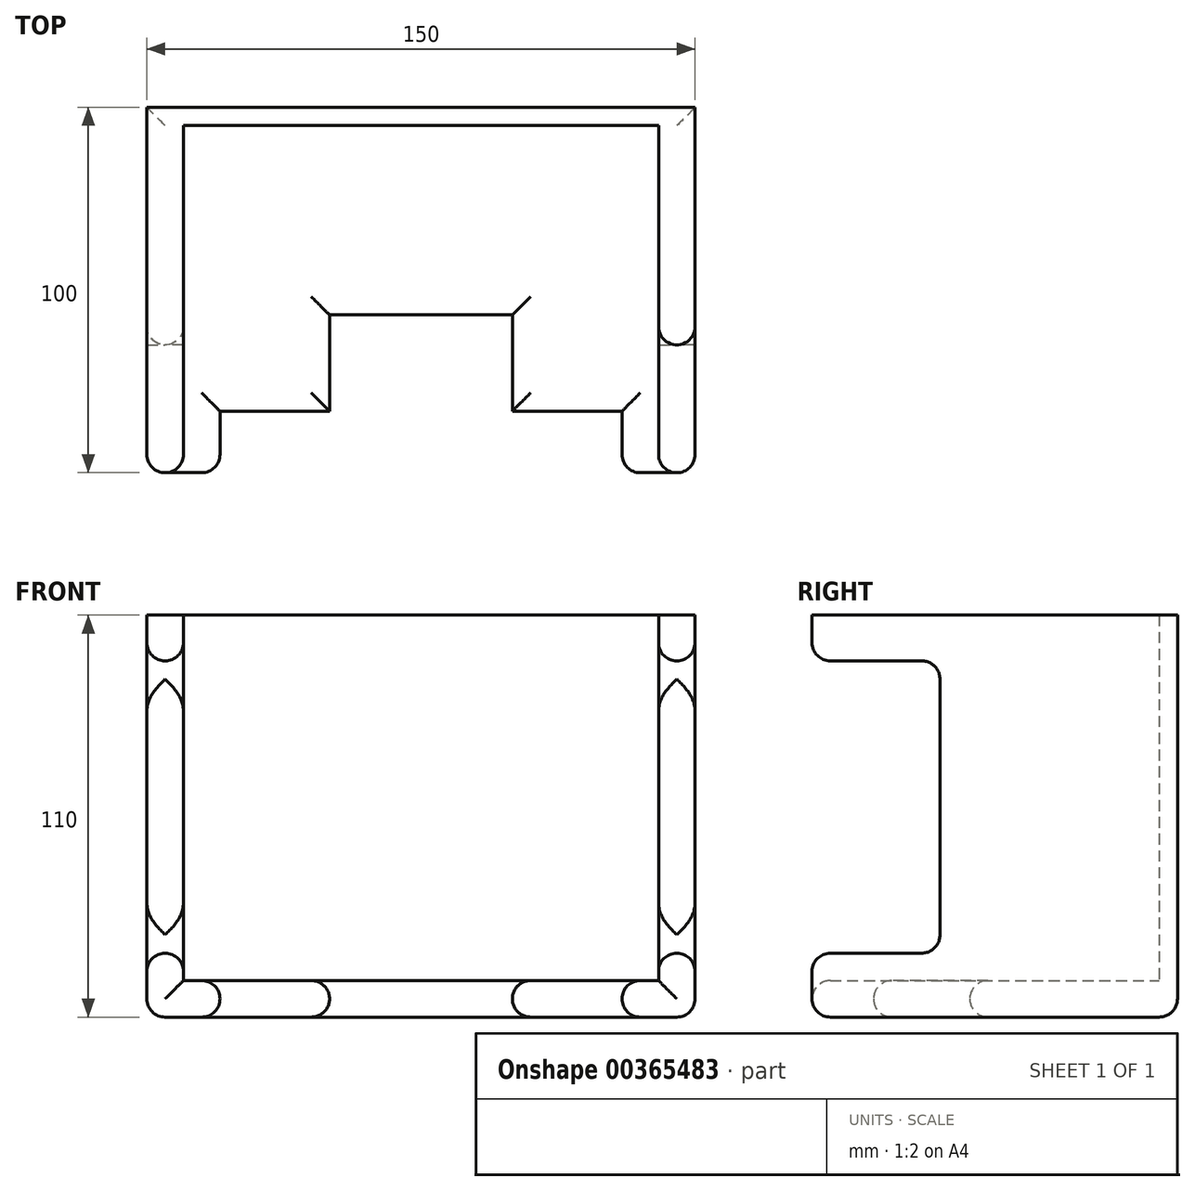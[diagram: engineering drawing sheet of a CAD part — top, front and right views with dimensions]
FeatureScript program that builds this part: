
annotation { "Feature Type Name" : "Feature", "Feature Type Description" : "" }
export const myFeature = defineFeature(function(context is Context, id is Id, definition is map)
    precondition{}
    {
        {
            var Q0;
            Q0=qCreatedBy(makeId("Front.planeOp"),FACE);
            var sketch = newSketch(context, id + "F0", { "sketchPlane" : qUnion([Q0])});
            skLineSegment(sketch, "E0", {"start": v(-43.91, 0) * mm, "end": v(-43.91, 100) * mm});
            skLineSegment(sketch, "E1", {"start": v(-43.91, 100) * mm, "end": v(-33.91, 100) * mm});
            skLineSegment(sketch, "E2", {"start": v(-33.91, 100) * mm, "end": v(-33.91, 0) * mm});
            skLineSegment(sketch, "E3", {"start": v(-33.91, 0) * mm, "end": v(-43.91, 0) * mm});
            skLineSegment(sketch, "E4", {"start": v(-33.91, 0) * mm, "end": v(96.09, 0) * mm});
            skLineSegment(sketch, "E5", {"start": v(96.09, 0) * mm, "end": v(106.09, 0) * mm});
            skLineSegment(sketch, "E6", {"start": v(106.09, 0) * mm, "end": v(106.09, 100) * mm});
            skLineSegment(sketch, "E7", {"start": v(106.09, 100) * mm, "end": v(96.09, 100) * mm});
            skLineSegment(sketch, "E8", {"start": v(96.09, 100) * mm, "end": v(96.09, 0) * mm});
            skLineSegment(sketch, "E9", {"start": v(-43.91, 0) * mm, "end": v(-43.91, -10) * mm});
            skLineSegment(sketch, "E10", {"start": v(-43.91, -10) * mm, "end": v(106.09, -10) * mm});
            skLineSegment(sketch, "E11", {"start": v(106.09, -10) * mm, "end": v(106.09, 0) * mm});
            skLineSegment(sketch, "E12", {"start": v(-33.91, 100) * mm, "end": v(96.09, 100) * mm});
            skSolve(sketch);
        }
        {
            var Q0;
            Q0=makeQuery(id+"F0.imprint","IMPRINT",FACE,{"disambiguationData":[TD([[makeQuery(id+"F0.imprint","IMPRINT",EDGE,{"derivedFrom":sQuery(id+"F0.wireOp",EDGE,"E2")}),1.0]])]});
            extrude(context, id + "F1", {"entities" : qUnion([Q0]), "depth" : 5 * mm});
        }
        {
            var Q0;
            Q0=makeQuery(id+"F0.imprint","IMPRINT",FACE,{"disambiguationData":[TD([[makeQuery(id+"F0.imprint","IMPRINT",EDGE,{"derivedFrom":sQuery(id+"F0.wireOp",EDGE,"E5")}),1.0]])]});
            var Q1;
            Q1=makeQuery(id+"F0.imprint","IMPRINT",FACE,{"disambiguationData":[TD([[makeQuery(id+"F0.imprint","IMPRINT",EDGE,{"derivedFrom":sQuery(id+"F0.wireOp",EDGE,"E3")}),1.0]])]});
            var Q2;
            Q2=makeQuery(id+"F0.imprint","IMPRINT",FACE,{"disambiguationData":[TD([[makeQuery(id+"F0.imprint","IMPRINT",EDGE,{"derivedFrom":sQuery(id+"F0.wireOp",EDGE,"E0")}),-1.0]])]});
            extrude(context, id + "F2", {"entities" : qUnion([Q0, Q1, Q2]), "operationType" : NewBodyOperationType.ADD, "depth" : 100 * mm});
        }
        {
            var Q0;
            Q0=makeQuery(id+"F2.opExtrude","SWEPT_FACE",FACE,{"disambiguationData":[OSD([sQuery(id+"F0.wireOp",EDGE,"E10")])]});
            var sketch = newSketch(context, id + "F3", { "sketchPlane" : qUnion([Q0])});
            skLineSegment(sketch, "E13.0.0", {"start": v(-43.91, 0) * mm, "end": v(106.09, 0) * mm});
            skLineSegment(sketch, "E13.0.1", {"start": v(106.09, 0) * mm, "end": v(106.09, 100) * mm});
            skLineSegment(sketch, "E13.0.2", {"start": v(106.09, 100) * mm, "end": v(-43.91, 100) * mm});
            skLineSegment(sketch, "E13.0.3", {"start": v(-43.91, 100) * mm, "end": v(-43.91, 0) * mm});
            skLineSegment(sketch, "E14", {"start": v(31.09, 100) * mm, "end": v(31.09, 0) * mm, "construction": true});
            skLineSegment(sketch, "E15", {"start": v(-43.91, 100) * mm, "end": v(-23.91, 100) * mm});
            skPoint(sketch, "E16.orphan", {"position": v(-23.91, 65.8) * mm});
            skPoint(sketch, "E17.orphan", {"position": v(86.09, 65.8) * mm});
            skPoint(sketch, "E18.orphan", {"position": v(106.09, 100) * mm});
            skPoint(sketch, "E19.orphan", {"position": v(31.09, 100) * mm});
            skLineSegment(sketch, "E20", {"start": v(6.09, 83.17) * mm, "end": v(6.09, 56.83) * mm});
            skLineSegment(sketch, "E21", {"start": v(6.09, 56.83) * mm, "end": v(31.09, 56.83) * mm});
            skLineSegment(sketch, "E22.MirrorCS", {"start": v(56.09, 56.83) * mm, "end": v(31.09, 56.83) * mm});
            skLineSegment(sketch, "E23.MirrorCS", {"start": v(56.09, 83.17) * mm, "end": v(56.09, 56.83) * mm});
            skLineSegment(sketch, "E24.MirrorCS", {"start": v(-23.91, 83.17) * mm, "end": v(-23.91, 100) * mm});
            skLineSegment(sketch, "E25.MirrorCS", {"start": v(-23.91, 83.17) * mm, "end": v(6.09, 83.17) * mm});
            skLineSegment(sketch, "E26.MirrorCS", {"start": v(86.09, 83.17) * mm, "end": v(86.09, 100) * mm});
            skLineSegment(sketch, "E27.MirrorCS", {"start": v(56.09, 83.17) * mm, "end": v(86.09, 83.17) * mm});
            skPoint(sketch, "E28.MirrorCS.start.orphan", {"position": v(86.09, 100) * mm});
            skSolve(sketch);
        }
        {
            var Q0;
            Q0=makeQuery(id+"F3.imprint","IMPRINT",FACE,{"disambiguationData":[TD([[makeQuery(id+"F3.imprint","IMPRINT",EDGE,{"derivedFrom":sQuery(id+"F3.wireOp",EDGE,"E20")}),1.0]])]});
            extrude(context, id + "F4", {"entities" : qUnion([Q0]), "operationType" : NewBodyOperationType.REMOVE, "oppositeDirection" : true, "depth" : 25 * mm});
        }
        {
            var Q0;
            Q0=makeQuery(id+"FPhnwHWxPQmKTOA_1.boolean.opBoolean","COPY",EDGE,{"derivedFrom":makeQuery(id+"FPhnwHWxPQmKTOA_1.opExtrude","CAP_EDGE",EDGE,{"disambiguationData":[OSD([sQuery(id+"F3.wireOp",EDGE,"E20")])],"isStart":true})});
            var Q1;
            Q1=makeQuery(id+"F2.opExtrude","SWEPT_FACE",FACE,{"disambiguationData":[OSD([sQuery(id+"F0.wireOp",EDGE,"E10")])]});
            var Q2;
            Q2=makeQuery(id+"F2.opExtrude","CAP_EDGE",EDGE,{"disambiguationData":[OSD([sQuery(id+"F0.wireOp",EDGE,"E0"),sQuery(id+"F0.wireOp",EDGE,"E9")])],"isStart":false});
            var Q3;
            Q3=makeQuery(id+"F2.opExtrude","CAP_EDGE",EDGE,{"disambiguationData":[OSD([sQuery(id+"F0.wireOp",EDGE,"E6"),sQuery(id+"F0.wireOp",EDGE,"E11")])],"isStart":false});
            var Q4;
            Q4=makeQuery(id+"F2.opExtrude","CAP_EDGE",EDGE,{"disambiguationData":[OSD([sQuery(id+"F0.wireOp",EDGE,"E2")])],"isStart":false});
            var Q5;
            Q5=makeQuery(id+"FPhnwHWxPQmKTOA_1.boolean.opBoolean","INTERSECT",EDGE,{"derivedFrom":[makeQuery(id+"F2.opExtrude","SWEPT_FACE",FACE,{"disambiguationData":[OSD([sQuery(id+"F0.wireOp",EDGE,"E4")])]}),makeQuery(id+"FPhnwHWxPQmKTOA_1.opExtrude","SWEPT_FACE",FACE,{"disambiguationData":[OSD([sQuery(id+"F3.wireOp",EDGE,"ktP89Wkd-3h25-mM1y-0ztc-tHv3V5rrrMsf")])]})]});
            var Q6;
            Q6=makeQuery(id+"FPhnwHWxPQmKTOA_1.boolean.opBoolean","INTERSECT",EDGE,{"derivedFrom":[makeQuery(id+"F2.opExtrude","SWEPT_FACE",FACE,{"disambiguationData":[OSD([sQuery(id+"F0.wireOp",EDGE,"E4")])]}),makeQuery(id+"FPhnwHWxPQmKTOA_1.opExtrude","SWEPT_FACE",FACE,{"disambiguationData":[OSD([sQuery(id+"F3.wireOp",EDGE,"bd52cf7c-c64b-48f8-b83b-5fc01dfa526b.trimOffspring")])]})]});
            var Q7;
            Q7=makeQuery(id+"FPhnwHWxPQmKTOA_1.boolean.opBoolean","INTERSECT",EDGE,{"derivedFrom":[makeQuery(id+"F2.opExtrude","SWEPT_FACE",FACE,{"disambiguationData":[OSD([sQuery(id+"F0.wireOp",EDGE,"E4")])]}),makeQuery(id+"FPhnwHWxPQmKTOA_1.opExtrude","SWEPT_FACE",FACE,{"disambiguationData":[OSD([sQuery(id+"F3.wireOp",EDGE,"E21"),sQuery(id+"F3.wireOp",EDGE,"E22.MirrorCS")])]})]});
            var Q8;
            {var subQ0=sQuery(id+"F0.wireOp",EDGE,"E4");var subQ1=sQuery(id+"F0.wireOp",EDGE,"E2");Q8=makeQuery(id+"FPhnwHWxPQmKTOA_1.boolean.opBoolean","SPLIT",EDGE,{"disambiguationData":[TD([makeQuery(id+"F2.opExtrude","SWEPT_FACE",FACE,{"disambiguationData":[OSD([subQ1])]})])],"derivedFrom":makeQuery(id+"F2.opExtrude","CAP_EDGE",EDGE,{"disambiguationData":[OSD([subQ0])],"isStart":false})});}
            var Q9;
            {var subQ0=sQuery(id+"F0.wireOp",EDGE,"E8");var subQ1=sQuery(id+"F0.wireOp",EDGE,"E4");Q9=makeQuery(id+"FPhnwHWxPQmKTOA_1.boolean.opBoolean","SPLIT",EDGE,{"disambiguationData":[TD([makeQuery(id+"F2.opExtrude","SWEPT_FACE",FACE,{"disambiguationData":[OSD([subQ0])]})])],"derivedFrom":makeQuery(id+"F2.opExtrude","CAP_EDGE",EDGE,{"disambiguationData":[OSD([subQ1])],"isStart":false})});}
            var Q10;
            Q10=makeQuery(id+"F2.opExtrude","CAP_EDGE",EDGE,{"disambiguationData":[OSD([sQuery(id+"F0.wireOp",EDGE,"E8")])],"isStart":false});
            fillet(context, id + "F5", {"entities" : qUnion([Q0, Q1, Q2, Q3, Q4, Q5, Q6, Q7, Q8, Q9, Q10]), "radius" : 5 * mm, "tangentPropagation" : true, "allowEdgeOverflow" : false});
        }
        {
            var Q0;
            Q0=makeQuery(id+"F2.opExtrude","SWEPT_FACE",FACE,{"disambiguationData":[OSD([sQuery(id+"F0.wireOp",EDGE,"E0"),sQuery(id+"F0.wireOp",EDGE,"E9")])]});
            var sketch = newSketch(context, id + "F6", { "sketchPlane" : qUnion([Q0])});
            skLineSegment(sketch, "E29.0.0", {"start": v(0, 100) * mm, "end": v(0, -5) * mm});
            skLineSegment(sketch, "E29.0.1", {"start": v(0, -5) * mm, "end": v(95, -5) * mm});
            skLineSegment(sketch, "E29.0.2", {"start": v(95, -5) * mm, "end": v(95, 7.5) * mm});
            skLineSegment(sketch, "E29.0.3", {"start": v(95, 100) * mm, "end": v(0, 100) * mm});
            skLineSegment(sketch, "E30.bottom", {"start": v(95, 47.5) * mm, "end": v(65, 47.5) * mm});
            skLineSegment(sketch, "E30.top", {"start": v(95, 7.5) * mm, "end": v(65, 7.5) * mm});
            skLineSegment(sketch, "E30.right", {"start": v(65, 47.5) * mm, "end": v(65, 7.5) * mm});
            skLineSegment(sketch, "E31", {"start": v(95, 47.5) * mm, "end": v(0, 47.5) * mm, "construction": true});
            skLineSegment(sketch, "E32.MirrorCS", {"start": v(65, 47.5) * mm, "end": v(65, 87.5) * mm});
            skLineSegment(sketch, "E33.MirrorCS", {"start": v(95, 87.5) * mm, "end": v(65, 87.5) * mm});
            skLineSegment(sketch, "E34.bottom", {"start": v(65, 87.5) * mm, "end": v(114.78, 87.5) * mm});
            skLineSegment(sketch, "E34.top", {"start": v(65, 7.5) * mm, "end": v(114.78, 7.5) * mm});
            skLineSegment(sketch, "E34.left", {"start": v(65, 87.5) * mm, "end": v(65, 7.5) * mm});
            skLineSegment(sketch, "E34.right", {"start": v(114.78, 87.5) * mm, "end": v(114.78, 7.5) * mm});
            skPoint(sketch, "E35.MirrorCS.end.orphan", {"position": v(95, 87.5) * mm});
            skPoint(sketch, "E35.MirrorCS.start.orphan", {"position": v(95, 47.5) * mm});
            skLineSegment(sketch, "E36.trimOffspring", {"start": v(95, 87.5) * mm, "end": v(95, 100) * mm});
            skSolve(sketch);
        }
        {
            var Q0;
            Q0=makeQuery(id+"F6.imprint","IMPRINT",FACE,{"disambiguationData":[TD([[makeQuery(id+"F6.imprint","IMPRINT",EDGE,{"derivedFrom":sQuery(id+"F6.wireOp",EDGE,"E30.bottom")}),1.0]])]});
            var Q1;
            {var subQ6=sQuery(id+"F6.wireOp",EDGE,"E34.right");Q1=makeQuery(id+"F6.imprint","IMPRINT",FACE,{"disambiguationData":[TD([[makeQuery(id+"F6.imprint","IMPRINT",EDGE,{"derivedFrom":subQ6}),-1.0]])]});}
            var Q2;
            {var subQ0=sQuery(id+"F6.wireOp",EDGE,"E30.bottom");Q2=makeQuery(id+"F6.imprint","IMPRINT",FACE,{"disambiguationData":[TD([[makeQuery(id+"F6.imprint","IMPRINT",EDGE,{"derivedFrom":subQ0}),-1.0]])]});}
            extrude(context, id + "F7", {"entities" : qUnion([Q0, Q1, Q2]), "operationType" : NewBodyOperationType.REMOVE, "endBound" : BoundingType.THROUGH_ALL, "oppositeDirection" : true, "depth" : 25 * mm});
        }
        {
            var Q0;
            Q0=makeQuery(id+"F7.boolean.opBoolean","INTERSECT",EDGE,{"derivedFrom":[makeQuery(id+"F2.opExtrude","SWEPT_FACE",FACE,{"disambiguationData":[OSD([sQuery(id+"F0.wireOp",EDGE,"E2")])]}),makeQuery(id+"F7.opExtrude","SWEPT_FACE",FACE,{"disambiguationData":[OSD([sQuery(id+"F6.wireOp",EDGE,"E34.left")])]})]});
            var Q1;
            Q1=makeQuery(id+"F7.boolean.opBoolean","INTERSECT",EDGE,{"derivedFrom":[makeQuery(id+"F2.opExtrude","SWEPT_FACE",FACE,{"disambiguationData":[OSD([sQuery(id+"F0.wireOp",EDGE,"E8")])]}),makeQuery(id+"F7.opExtrude","SWEPT_FACE",FACE,{"disambiguationData":[OSD([sQuery(id+"F6.wireOp",EDGE,"E34.left")])]})]});
            var Q2;
            Q2=makeQuery(id+"F7.boolean.opBoolean","INTERSECT",EDGE,{"derivedFrom":[makeQuery(id+"F2.opExtrude","SWEPT_FACE",FACE,{"disambiguationData":[OSD([sQuery(id+"F0.wireOp",EDGE,"E6"),sQuery(id+"F0.wireOp",EDGE,"E11")])]}),makeQuery(id+"F7.opExtrude","SWEPT_FACE",FACE,{"disambiguationData":[OSD([sQuery(id+"F6.wireOp",EDGE,"E34.left")])]})]});
            var Q3;
            Q3=makeQuery(id+"F7.boolean.opBoolean","COPY",EDGE,{"derivedFrom":makeQuery(id+"F7.opExtrude","CAP_EDGE",EDGE,{"disambiguationData":[OSD([sQuery(id+"F6.wireOp",EDGE,"E34.left")])],"isStart":true})});
            var Q4;
            {var subQ0=sQuery(id+"F0.wireOp",EDGE,"E2");Q4=makeQuery(id+"F7.boolean.opBoolean","COPY",FACE,{"disambiguationData":[TD([makeQuery(id+"F2.opExtrude","SWEPT_FACE",FACE,{"disambiguationData":[OSD([subQ0])]})])],"derivedFrom":makeQuery(id+"F7.opExtrude","SWEPT_FACE",FACE,{"disambiguationData":[OSD([sQuery(id+"F6.wireOp",EDGE,"E34.bottom")])]})});}
            var Q5;
            {var subQ0=sQuery(id+"F0.wireOp",EDGE,"E2");Q5=makeQuery(id+"F7.boolean.opBoolean","COPY",FACE,{"disambiguationData":[TD([makeQuery(id+"F2.opExtrude","SWEPT_FACE",FACE,{"disambiguationData":[OSD([subQ0])]})])],"derivedFrom":makeQuery(id+"F7.opExtrude","SWEPT_FACE",FACE,{"disambiguationData":[OSD([sQuery(id+"F6.wireOp",EDGE,"E34.top")])]})});}
            var Q6;
            Q6=makeQuery(id+"F7.boolean.opBoolean","INTERSECT",EDGE,{"derivedFrom":[makeQuery(id+"F5.opFillet","BLEND_FACE",FACE,{"disambiguationData":[OSD([sQuery(id+"F0.wireOp",EDGE,"E8")])]}),makeQuery(id+"F7.opExtrude","SWEPT_FACE",FACE,{"disambiguationData":[OSD([sQuery(id+"F6.wireOp",EDGE,"E34.bottom")])]})]});
            var Q7;
            {var subQ0=sQuery(id+"F0.wireOp",EDGE,"E8");Q7=makeQuery(id+"F7.boolean.opBoolean","COPY",FACE,{"disambiguationData":[TD([makeQuery(id+"F2.opExtrude","SWEPT_FACE",FACE,{"disambiguationData":[OSD([subQ0])]})])],"derivedFrom":makeQuery(id+"F7.opExtrude","SWEPT_FACE",FACE,{"disambiguationData":[OSD([sQuery(id+"F6.wireOp",EDGE,"E34.top")])]})});}
            var Q8;
            {var subQ0=sQuery(id+"F0.wireOp",EDGE,"E8");Q8=makeQuery(id+"F7.boolean.opBoolean","COPY",FACE,{"disambiguationData":[TD([makeQuery(id+"F2.opExtrude","SWEPT_FACE",FACE,{"disambiguationData":[OSD([subQ0])]})])],"derivedFrom":makeQuery(id+"F7.opExtrude","SWEPT_FACE",FACE,{"disambiguationData":[OSD([sQuery(id+"F6.wireOp",EDGE,"E34.bottom")])]})});}
            var Q9;
            Q9=makeQuery(id+"F4.boolean.opBoolean","INTERSECT",EDGE,{"derivedFrom":[makeQuery(id+"F2.opExtrude","SWEPT_FACE",FACE,{"disambiguationData":[OSD([sQuery(id+"F0.wireOp",EDGE,"E4")])]}),makeQuery(id+"F4.opExtrude","SWEPT_FACE",FACE,{"disambiguationData":[OSD([sQuery(id+"F3.wireOp",EDGE,"E21"),sQuery(id+"F3.wireOp",EDGE,"E22.MirrorCS")])]})]});
            var Q10;
            Q10=makeQuery(id+"F4.boolean.opBoolean","INTERSECT",EDGE,{"derivedFrom":[makeQuery(id+"F2.opExtrude","SWEPT_FACE",FACE,{"disambiguationData":[OSD([sQuery(id+"F0.wireOp",EDGE,"E4")])]}),makeQuery(id+"F4.opExtrude","SWEPT_FACE",FACE,{"disambiguationData":[OSD([sQuery(id+"F3.wireOp",EDGE,"E27.MirrorCS")])]})]});
            var Q11;
            Q11=makeQuery(id+"F4.boolean.opBoolean","INTERSECT",EDGE,{"derivedFrom":[makeQuery(id+"F2.opExtrude","SWEPT_FACE",FACE,{"disambiguationData":[OSD([sQuery(id+"F0.wireOp",EDGE,"E4")])]}),makeQuery(id+"F4.opExtrude","SWEPT_FACE",FACE,{"disambiguationData":[OSD([sQuery(id+"F3.wireOp",EDGE,"E23.MirrorCS")])]})]});
            var Q12;
            Q12=makeQuery(id+"F4.boolean.opBoolean","INTERSECT",EDGE,{"derivedFrom":[makeQuery(id+"F2.opExtrude","SWEPT_FACE",FACE,{"disambiguationData":[OSD([sQuery(id+"F0.wireOp",EDGE,"E4")])]}),makeQuery(id+"F4.opExtrude","SWEPT_FACE",FACE,{"disambiguationData":[OSD([sQuery(id+"F3.wireOp",EDGE,"E26.MirrorCS")])]})]});
            var Q13;
            Q13=makeQuery(id+"F4.boolean.opBoolean","INTERSECT",EDGE,{"derivedFrom":[makeQuery(id+"F2.opExtrude","SWEPT_FACE",FACE,{"disambiguationData":[OSD([sQuery(id+"F0.wireOp",EDGE,"E4")])]}),makeQuery(id+"F4.opExtrude","SWEPT_FACE",FACE,{"disambiguationData":[OSD([sQuery(id+"F3.wireOp",EDGE,"E24.MirrorCS")])]})]});
            var Q14;
            Q14=makeQuery(id+"F4.boolean.opBoolean","INTERSECT",EDGE,{"derivedFrom":[makeQuery(id+"F2.opExtrude","SWEPT_FACE",FACE,{"disambiguationData":[OSD([sQuery(id+"F0.wireOp",EDGE,"E4")])]}),makeQuery(id+"F4.opExtrude","SWEPT_FACE",FACE,{"disambiguationData":[OSD([sQuery(id+"F3.wireOp",EDGE,"E25.MirrorCS")])]})]});
            var Q15;
            Q15=makeQuery(id+"F4.boolean.opBoolean","INTERSECT",EDGE,{"derivedFrom":[makeQuery(id+"F2.opExtrude","SWEPT_FACE",FACE,{"disambiguationData":[OSD([sQuery(id+"F0.wireOp",EDGE,"E4")])]}),makeQuery(id+"F4.opExtrude","SWEPT_FACE",FACE,{"disambiguationData":[OSD([sQuery(id+"F3.wireOp",EDGE,"E20")])]})]});
            fillet(context, id + "F8", {"entities" : qUnion([Q0, Q1, Q2, Q3, Q4, Q5, Q6, Q7, Q8, Q9, Q10, Q11, Q12, Q13, Q14, Q15]), "radius" : 5 * mm, "tangentPropagation" : true, "allowEdgeOverflow" : false});
        }
    });
